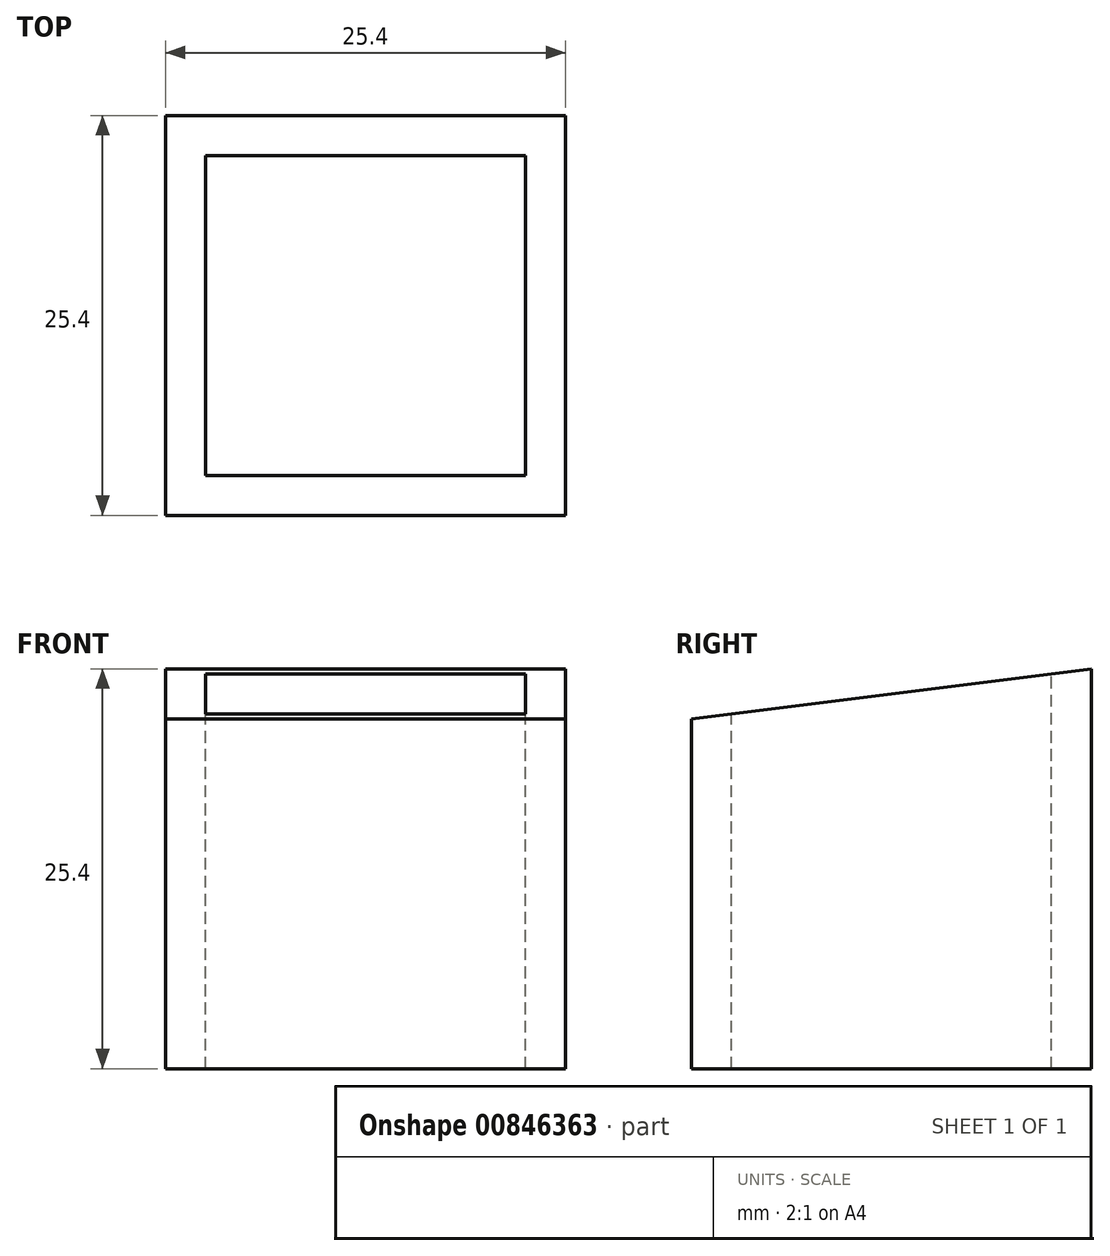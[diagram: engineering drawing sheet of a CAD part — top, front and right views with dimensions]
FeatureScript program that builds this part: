
annotation { "Feature Type Name" : "Feature", "Feature Type Description" : "" }
export const myFeature = defineFeature(function(context is Context, id is Id, definition is map)
    precondition{}
    {
        {
            var Q0;
            Q0=qCreatedBy(makeId("Front.planeOp"),FACE);
            var sketch = newSketch(context, id + "F0", { "sketchPlane" : qUnion([Q0])});
            skLineSegment(sketch, "E0.bottom", {"start": v(12.7, -12.7) * mm, "end": v(-12.7, -12.7) * mm});
            skLineSegment(sketch, "E0.top", {"start": v(12.7, 12.7) * mm, "end": v(-12.7, 12.7) * mm});
            skLineSegment(sketch, "E0.left", {"start": v(12.7, -12.7) * mm, "end": v(12.7, 12.7) * mm});
            skLineSegment(sketch, "E0.right", {"start": v(-12.7, -12.7) * mm, "end": v(-12.7, 12.7) * mm});
            skPoint(sketch, "E0.middle", {"position": v(0, 0) * mm});
            skSolve(sketch);
        }
        {
            var Q0;
            Q0=makeQuery(id+"F0.imprint","IMPRINT",FACE,{"disambiguationData":[TD([[makeQuery(id+"F0.imprint","IMPRINT",EDGE,{"derivedFrom":sQuery(id+"F0.wireOp",EDGE,"E0.bottom")}),-1.0]])]});
            extrude(context, id + "F1", {"entities" : qUnion([Q0]), "endBound" : BoundingType.SYMMETRIC, "depth" : 25.4 * mm, "offsetDistance" : 25 * mm});
        }
        {
            var Q0;
            Q0=makeQuery(id+"F1.opExtrude","SWEPT_FACE",FACE,{"disambiguationData":[OSD([sQuery(id+"F0.wireOp",EDGE,"E0.top")])]});
            var Q1;
            Q1=makeQuery(id+"F1.opExtrude","SWEPT_FACE",FACE,{"disambiguationData":[OSD([sQuery(id+"F0.wireOp",EDGE,"E0.bottom")])]});
            shell(context, id + "F2", {"entities" : qUnion([Q0, Q1]), "thickness" : 2.54 * mm});
        }
        {
            var Q0;
            Q0=makeQuery(id+"F1.opExtrude","SWEPT_FACE",FACE,{"disambiguationData":[OSD([sQuery(id+"F0.wireOp",EDGE,"E0.left")])]});
            var sketch = newSketch(context, id + "F3", { "sketchPlane" : qUnion([Q0])});
            skLineSegment(sketch, "E1", {"start": v(-12.7, 9.53) * mm, "end": v(12.7, 12.7) * mm});
            skLineSegment(sketch, "E2", {"start": v(12.7, 12.7) * mm, "end": v(-12.7, 12.7) * mm});
            skLineSegment(sketch, "E3", {"start": v(-12.7, 12.7) * mm, "end": v(-12.7, 9.52) * mm});
            skSolve(sketch);
        }
        {
            var Q0;
            Q0=makeQuery(id+"F3.imprint","IMPRINT",FACE,{"disambiguationData":[TD([[makeQuery(id+"F3.imprint","IMPRINT",EDGE,{"derivedFrom":sQuery(id+"F3.wireOp",EDGE,"E1")}),1.0]])]});
            extrude(context, id + "F4", {"entities" : qUnion([Q0]), "operationType" : NewBodyOperationType.REMOVE, "endBound" : BoundingType.THROUGH_ALL, "oppositeDirection" : true, "depth" : 25.4 * mm, "offsetDistance" : 25.4 * mm});
        }
    });
